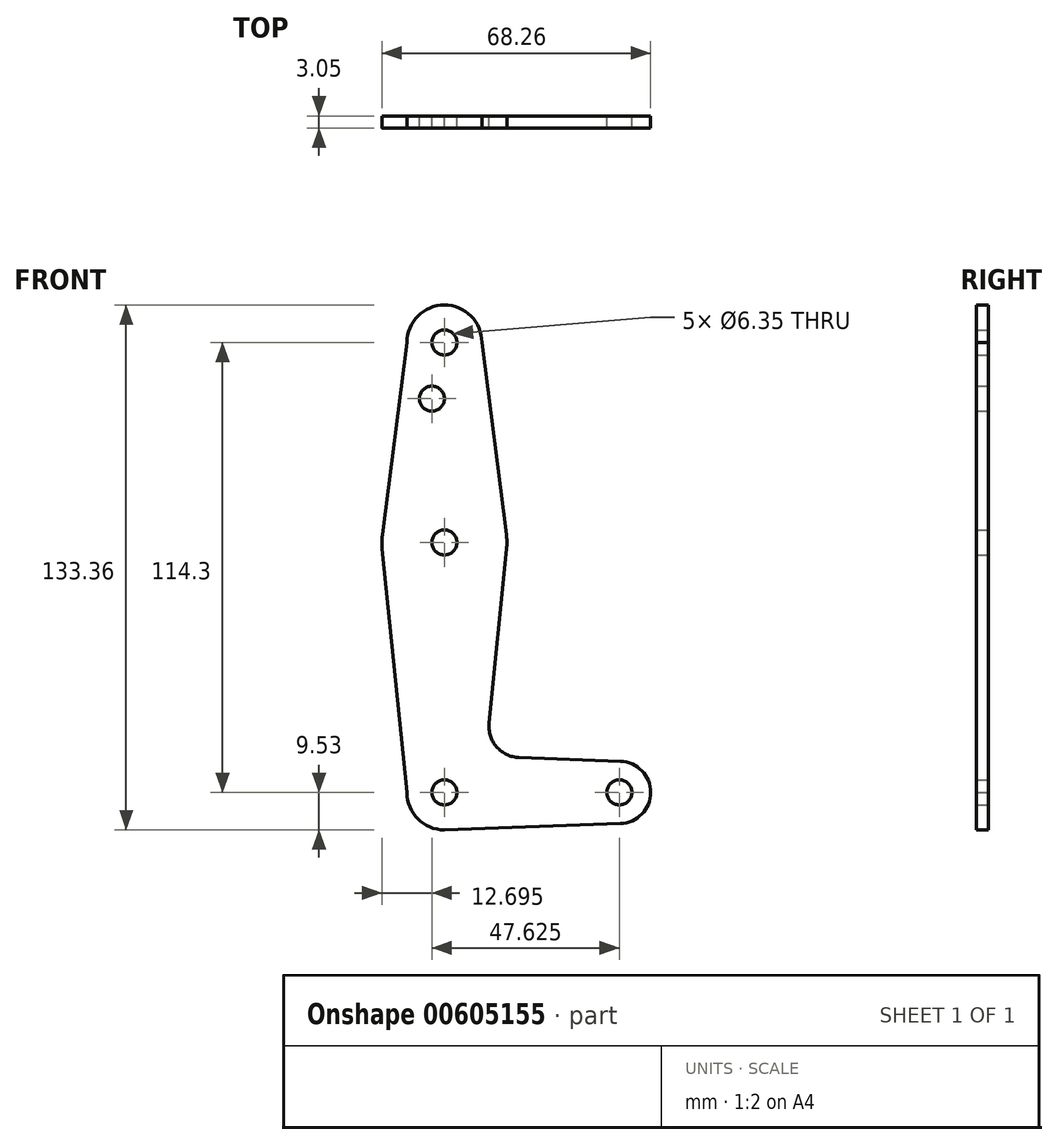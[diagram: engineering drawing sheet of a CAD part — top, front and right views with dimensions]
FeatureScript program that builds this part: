
annotation { "Feature Type Name" : "Feature", "Feature Type Description" : "" }
export const myFeature = defineFeature(function(context is Context, id is Id, definition is map)
    precondition{}
    {
        {
            var Q0;
            Q0=qCreatedBy(makeId("Front.planeOp"),FACE);
            var sketch = newSketch(context, id + "F0", { "sketchPlane" : qUnion([Q0])});
            skCircle(sketch, "E0", {"center": v(0, 0) * mm, "radius": 9.53 * mm});
            skCircle(sketch, "E1", {"center": v(44.45, 0) * mm, "radius": 7.94 * mm});
            skCircle(sketch, "E2", {"center": v(0, 63.5) * mm, "radius": 15.88 * mm});
            skCircle(sketch, "E3", {"center": v(0, 114.3) * mm, "radius": 9.53 * mm});
            skLineSegment(sketch, "E4", {"start": v(0, 0) * mm, "end": v(44.45, 0) * mm, "construction": true});
            skLineSegment(sketch, "E5", {"start": v(0, 0) * mm, "end": v(0, 114.3) * mm, "construction": true});
            skLineSegment(sketch, "E6", {"start": v(-9.52, 0) * mm, "end": v(-15.8, 61.9) * mm});
            skLineSegment(sketch, "E7", {"start": v(15.8, 61.9) * mm, "end": v(11.34, 17.6) * mm});
            skLineSegment(sketch, "E8", {"start": v(-9.53, 114.3) * mm, "end": v(-15.75, 65.5) * mm});
            skLineSegment(sketch, "E9", {"start": v(9.53, 114.3) * mm, "end": v(15.75, 65.5) * mm});
            skLineSegment(sketch, "E10", {"start": v(0, -9.52) * mm, "end": v(44.73, -7.93) * mm});
            skLineSegment(sketch, "E11", {"start": v(18.97, 8.85) * mm, "end": v(44.73, 7.93) * mm});
            skCircle(sketch, "E12", {"center": v(44.45, 0) * mm, "radius": 3.18 * mm});
            skCircle(sketch, "E13", {"center": v(0, 0) * mm, "radius": 3.18 * mm});
            skCircle(sketch, "E14", {"center": v(0, 63.5) * mm, "radius": 3.18 * mm});
            skCircle(sketch, "E15", {"center": v(-3.18, 100.03) * mm, "radius": 3.18 * mm});
            skCircle(sketch, "E16", {"center": v(0, 114.3) * mm, "radius": 3.18 * mm});
            skArc(sketch, "E17.filletArc", {"start": v(11.34, 17.6) * mm, "mid": v(13.26, 11.57) * mm, "end": v(18.97, 8.85) * mm});
            skSolve(sketch);
        }
        {
            var Q0;
            {var subQ1=sQuery(id+"F0.wireOp",EDGE,"E8");Q0=makeQuery(id+"F0.imprint","IMPRINT",FACE,{"disambiguationData":[TD([[makeQuery(id+"F0.imprint","IMPRINT",EDGE,{"derivedFrom":subQ1}),1.0]])]});}
            var Q1;
            Q1=makeQuery(id+"F0.imprint","IMPRINT",FACE,{"disambiguationData":[TD([[makeQuery(id+"F0.imprint","IMPRINT",EDGE,{"derivedFrom":sQuery(id+"F0.wireOp",EDGE,"E16")}),-1.0]])]});
            var Q2;
            Q2=makeQuery(id+"F0.imprint","IMPRINT",FACE,{"disambiguationData":[TD([[makeQuery(id+"F0.imprint","IMPRINT",EDGE,{"derivedFrom":sQuery(id+"F0.wireOp",EDGE,"E14")}),-1.0]])]});
            var Q3;
            {var subQ0=sQuery(id+"F0.wireOp",EDGE,"E6");Q3=makeQuery(id+"F0.imprint","IMPRINT",FACE,{"disambiguationData":[TD([[makeQuery(id+"F0.imprint","IMPRINT",EDGE,{"derivedFrom":subQ0}),-1.0]])]});}
            var Q4;
            Q4=makeQuery(id+"F0.imprint","IMPRINT",FACE,{"disambiguationData":[TD([[makeQuery(id+"F0.imprint","IMPRINT",EDGE,{"derivedFrom":sQuery(id+"F0.wireOp",EDGE,"E13")}),-1.0]])]});
            var Q5;
            Q5=makeQuery(id+"F0.imprint","IMPRINT",FACE,{"disambiguationData":[TD([[makeQuery(id+"F0.imprint","IMPRINT",EDGE,{"derivedFrom":sQuery(id+"F0.wireOp",EDGE,"E12")}),-1.0]])]});
            extrude(context, id + "F1", {"entities" : qUnion([Q0, Q1, Q2, Q3, Q4, Q5]), "depth" : 3.05 * mm, "offsetDistance" : 25.4 * mm});
        }
    });
